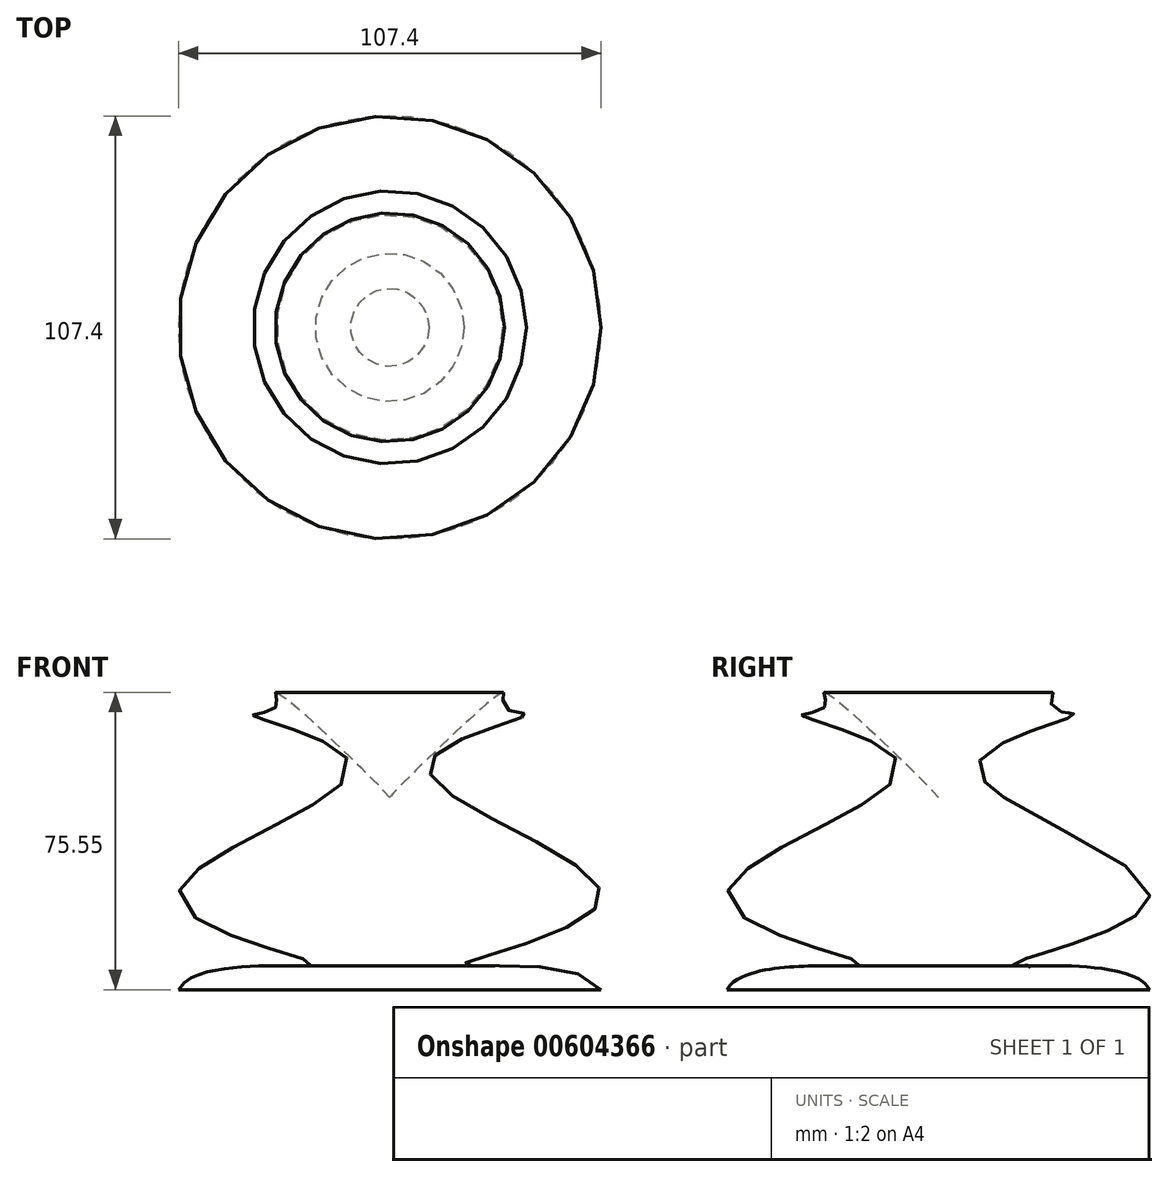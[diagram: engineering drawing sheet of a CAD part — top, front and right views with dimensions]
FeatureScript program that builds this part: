
annotation { "Feature Type Name" : "Feature", "Feature Type Description" : "" }
export const myFeature = defineFeature(function(context is Context, id is Id, definition is map)
    precondition{}
    {
        {
            var Q0;
            Q0=qCreatedBy(makeId("Front.planeOp"),FACE);
            var sketch = newSketch(context, id + "F0", { "sketchPlane" : qUnion([Q0])});
            skLineSegment(sketch, "E0", {"start": v(0, 0) * mm, "end": v(53.68, 0) * mm});
            skFitSpline(sketch, "E1", {"points": [v(53.68, 0) * mm, v(18.85, 6.48) * mm, v(53.68, 23.46) * mm, v(9.93, 56.55) * mm, v(34.68, 69.8) * mm, v(28.92, 71.8) * mm, v(28.92, 75.55) * mm, v(0, 48.78) * mm, v(0, 48.5) * mm], "startDerivative": vector(-77.54, 156.9) * mm, "endDerivative": vector(12.04, -18.6) * mm});
            skLineSegment(sketch, "E2", {"start": v(0, 48.78) * mm, "end": v(0, 0) * mm});
            skSolve(sketch);
        }
        {
            var Q0;
            {var subQ0=sQuery(id+"F0.wireOp",EDGE,"E0");Q0=makeQuery(id+"F0.imprint","IMPRINT",FACE,{"disambiguationData":[TD([[makeQuery(id+"F0.imprint","IMPRINT",EDGE,{"derivedFrom":subQ0}),1.0]])]});}
            var Q1;
            Q1=sQuery(id+"F0.wireOp",EDGE,"E2");
            revolve(context, id + "F1", {"entities" : qUnion([Q0]), "axis" : qUnion([Q1]), "revolveType" : RevolveType.FULL});
        }
    });
